# Revit family: 3238 Armchair THE SPANISH DINING CHAIR
name_source: partatom
category: Furniture
revit_build: Autodesk Revit 2017 (Build: 20171027_0315(x64)
units: mm (PartAtom-declared; Revit-internal decimal feet)

## family parameters
Always vertical = Yes
Cut with Voids When Loaded = No
OmniClass Number = 23.40.20.00
OmniClass Title = General Furniture and Specialties
Room Calculation Point = No
Shared = No
Work Plane-Based = No

## types (1)
- 3238 Armchair THE SPANISH DINING CHAIR
    Armrest = FF Oak Soap vertical
    Backrest = FF Natural Saddle Leather
    Depth = 48 cm
    Description = The Spanish Dining Chair is a testament to the application of honest materials. Crafted from the finest selection of oak and flawless saddle leather, the chair is available with or without armrests, and with multiple finishes from light to darker shades, depending on the atmosphere you want to create.
    Design year = 1964
    Frame Horizontal = FF Oak Soap horizontal
    Frame Vertical = FF Oak Soap vertical
    Height = 84,5 cm
    Item No. = 3238
    Legs = FF Oak Soap vertical
    Manufacturer = Fredericia Furniture
    Model = Armchair THE SPANISH DINING CHAIR
    Seat = FF Natural Saddle Leather
    Seat Height = 46 cm
    URL = https://www.fredericia.com
    Variation Legs - Extra charge = Available in other kinds of wood
    Variation Legs - Standard = Available in other kinds of wood
    Variations Gliders = Available with glides with or without felt
    Variations Seat - Backrest = Available in other kinds of saddle leather
    Weight = 8 kg
    Width = 64,5 cm

## geometry (parser evidence)
native form markers: Sweep x2
no freeform markers — native parametric forms only
